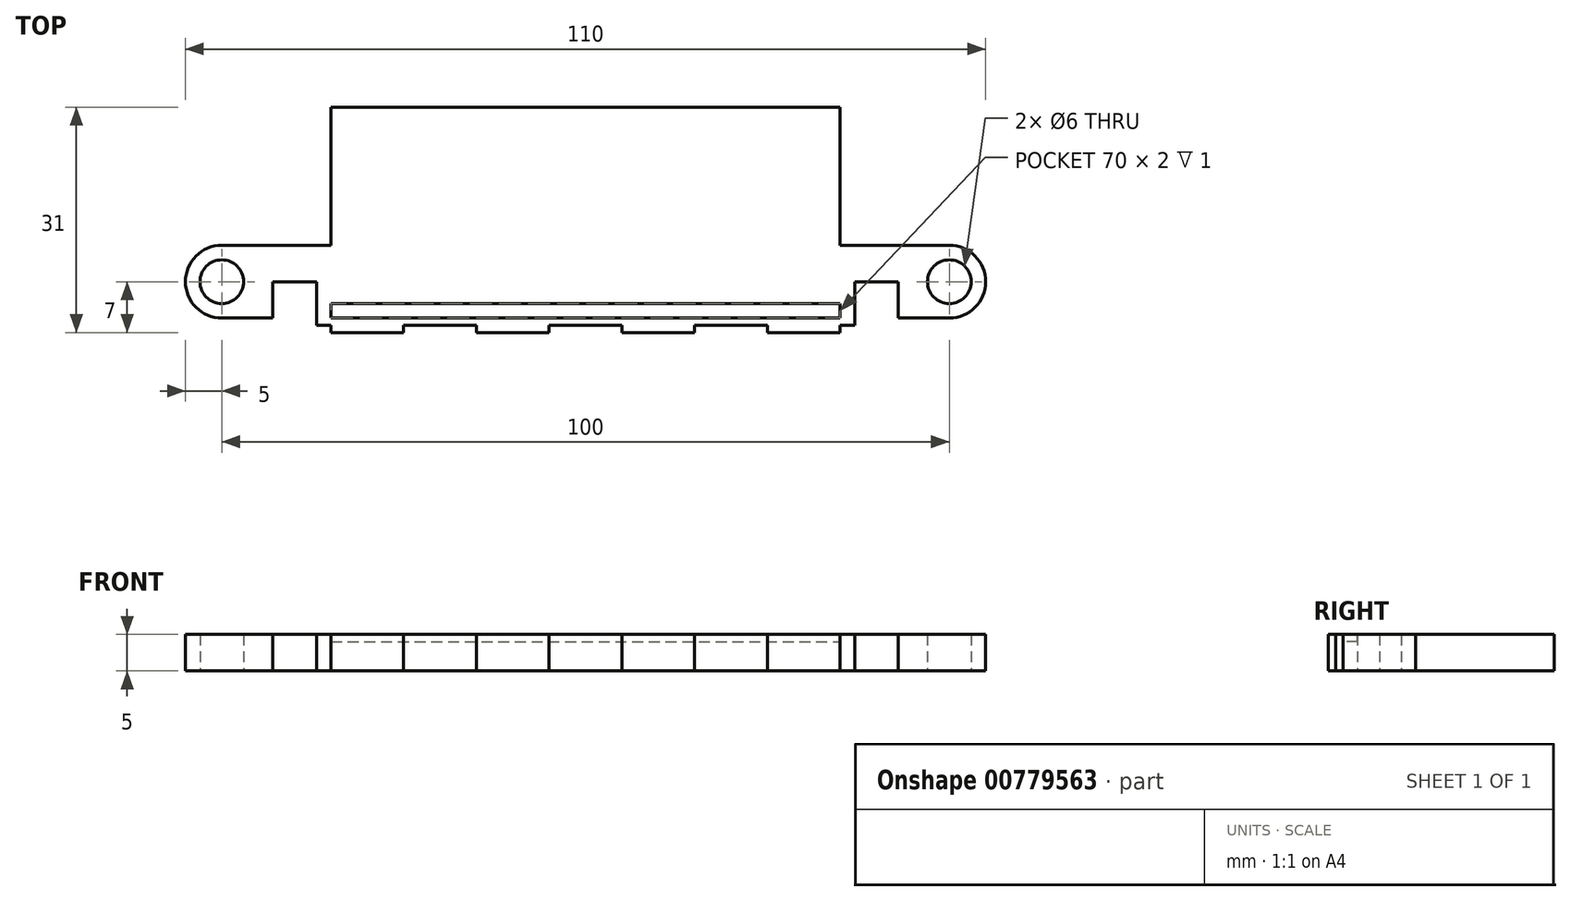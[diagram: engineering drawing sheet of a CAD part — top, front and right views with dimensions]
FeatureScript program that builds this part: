
annotation { "Feature Type Name" : "Feature", "Feature Type Description" : "" }
export const myFeature = defineFeature(function(context is Context, id is Id, definition is map)
    precondition{}
    {
        {
            assignVariable(context, id + "F0", {"name" : "MDF_thickness", "anyValue" : 5});
        }
        {
            var Q0;
            Q0=qCreatedBy(makeId("Top.planeOp"),FACE);
            var sketch = newSketch(context, id + "F1", { "sketchPlane" : qUnion([Q0])});
            skLineSegment(sketch, "E0.left", {"start": v(35, -16) * mm, "end": v(35, 15) * mm, "construction": true});
            skLineSegment(sketch, "E1", {"start": v(0, -15) * mm, "end": v(5, -15) * mm});
            skLineSegment(sketch, "E2", {"start": v(5, -15) * mm, "end": v(5, -16) * mm});
            skLineSegment(sketch, "E3", {"start": v(5, -16) * mm, "end": v(15, -16) * mm});
            skLineSegment(sketch, "E4", {"start": v(15, -16) * mm, "end": v(15, -15) * mm});
            skLineSegment(sketch, "E5", {"start": v(15, -15) * mm, "end": v(25, -15) * mm});
            skLineSegment(sketch, "E6", {"start": v(25, -15) * mm, "end": v(25, -16) * mm});
            skLineSegment(sketch, "E7", {"start": v(25, -16) * mm, "end": v(35, -16) * mm});
            skLineSegment(sketch, "E8", {"start": v(35, -16) * mm, "end": v(35, -15) * mm});
            skArc(sketch, "E9", {"start": v(50, -14) * mm, "mid": v(55, -9) * mm, "end": v(50, -4) * mm});
            skCircle(sketch, "E10", {"center": v(50, -9) * mm, "radius": 3 * mm});
            skLineSegment(sketch, "E11", {"start": v(50, -4) * mm, "end": v(35, -4) * mm});
            skLineSegment(sketch, "E12", {"start": v(45, -4) * mm, "end": v(45, -14) * mm, "construction": true});
            skLineSegment(sketch, "E13", {"start": v(35, -4) * mm, "end": v(35, 15) * mm});
            skLineSegment(sketch, "E14", {"start": v(35, 15) * mm, "end": v(0, 15) * mm});
            skLineSegment(sketch, "E15", {"start": v(50, -14) * mm, "end": v(45, -14) * mm});
            skLineSegment(sketch, "E16", {"start": v(45, -14) * mm, "end": v(43, -14) * mm});
            skLineSegment(sketch, "E17", {"start": v(43, -14) * mm, "end": v(43, -9) * mm});
            skLineSegment(sketch, "E18", {"start": v(43, -9) * mm, "end": v(37, -9) * mm});
            skLineSegment(sketch, "E19", {"start": v(37, -9) * mm, "end": v(37, -14) * mm});
            skLineSegment(sketch, "E20", {"start": v(35, -15) * mm, "end": v(37, -15) * mm});
            skLineSegment(sketch, "E21", {"start": v(37, -15) * mm, "end": v(37, -14) * mm});
            skLineSegment(sketch, "E22.MirrorCS", {"start": v(-35, 15) * mm, "end": v(0, 15) * mm});
            skLineSegment(sketch, "E23.MirrorCS", {"start": v(0, -15) * mm, "end": v(-5, -15) * mm});
            skLineSegment(sketch, "E24.MirrorCS", {"start": v(-35, -16) * mm, "end": v(-35, -15) * mm});
            skLineSegment(sketch, "E25.MirrorCS", {"start": v(-35, -15) * mm, "end": v(-37, -15) * mm});
            skLineSegment(sketch, "E26.MirrorCS", {"start": v(-45, -14) * mm, "end": v(-43, -14) * mm});
            skLineSegment(sketch, "E27.MirrorCS", {"start": v(-15, -16) * mm, "end": v(-15, -15) * mm});
            skLineSegment(sketch, "E28.MirrorCS", {"start": v(-37, -15) * mm, "end": v(-37, -14) * mm});
            skLineSegment(sketch, "E29.MirrorCS", {"start": v(-25, -15) * mm, "end": v(-25, -16) * mm});
            skLineSegment(sketch, "E30.MirrorCS", {"start": v(-5, -15) * mm, "end": v(-5, -16) * mm});
            skLineSegment(sketch, "E31.MirrorCS", {"start": v(-50, -14) * mm, "end": v(-45, -14) * mm});
            skLineSegment(sketch, "E32.MirrorCS", {"start": v(-35, -4) * mm, "end": v(-35, 15) * mm});
            skArc(sketch, "E33.MirrorCS", {"start": v(-50, -14) * mm, "mid": v(-55, -9) * mm, "end": v(-50, -4) * mm});
            skLineSegment(sketch, "E34.MirrorCS", {"start": v(-5, -16) * mm, "end": v(-15, -16) * mm});
            skLineSegment(sketch, "E35.MirrorCS", {"start": v(-45, -4) * mm, "end": v(-45, -14) * mm, "construction": true});
            skLineSegment(sketch, "E36.MirrorCS", {"start": v(-35, -16) * mm, "end": v(-35, 15) * mm, "construction": true});
            skLineSegment(sketch, "E37.MirrorCS", {"start": v(-15, -15) * mm, "end": v(-25, -15) * mm});
            skLineSegment(sketch, "E38.MirrorCS", {"start": v(-25, -16) * mm, "end": v(-35, -16) * mm});
            skLineSegment(sketch, "E39.MirrorCS", {"start": v(-43, -9) * mm, "end": v(-37, -9) * mm});
            skLineSegment(sketch, "E40.MirrorCS", {"start": v(-37, -9) * mm, "end": v(-37, -14) * mm});
            skCircle(sketch, "E41.MirrorC", {"center": v(-50, -9) * mm, "radius": 3 * mm});
            skLineSegment(sketch, "E42.MirrorCS", {"start": v(-50, -4) * mm, "end": v(-35, -4) * mm});
            skLineSegment(sketch, "E43.MirrorCS", {"start": v(-43, -14) * mm, "end": v(-43, -9) * mm});
            skSolve(sketch);
        }
        {
            var Q0;
            Q0 = qSketchRegion(id + "F1", true);
            extrude(context, id + "F2", {"entities" : qUnion([Q0]), "depth" : (getVariable(context, 'MDF_thickness')) * mm, "offsetDistance" : 25 * mm});
        }
        {
            var Q0;
            Q0=makeQuery(id+"F2.opExtrude","CAP_FACE",FACE,{"disambiguationData":[OSD([sQuery(id+"F1.wireOp",EDGE,"E1"),sQuery(id+"F1.wireOp",EDGE,"E2"),sQuery(id+"F1.wireOp",EDGE,"E3"),sQuery(id+"F1.wireOp",EDGE,"E4"),sQuery(id+"F1.wireOp",EDGE,"E5"),sQuery(id+"F1.wireOp",EDGE,"E6"),sQuery(id+"F1.wireOp",EDGE,"E7"),sQuery(id+"F1.wireOp",EDGE,"E8"),sQuery(id+"F1.wireOp",EDGE,"E9"),sQuery(id+"F1.wireOp",EDGE,"E10"),sQuery(id+"F1.wireOp",EDGE,"E11"),sQuery(id+"F1.wireOp",EDGE,"E13"),sQuery(id+"F1.wireOp",EDGE,"E14"),sQuery(id+"F1.wireOp",EDGE,"E15"),sQuery(id+"F1.wireOp",EDGE,"E16"),sQuery(id+"F1.wireOp",EDGE,"E17"),sQuery(id+"F1.wireOp",EDGE,"E18"),sQuery(id+"F1.wireOp",EDGE,"E19"),sQuery(id+"F1.wireOp",EDGE,"oVFt1hSz-rF75-tQqa-whk6-lmqHoJ6cugXr"),sQuery(id+"F1.wireOp",EDGE,"75e155fa-2116-4a00-8d93-47b2ce3b5e2c0.MirrorCS"),sQuery(id+"F1.wireOp",EDGE,"75e155fa-2116-4a00-8d93-47b2ce3b5e2c1.MirrorCS"),sQuery(id+"F1.wireOp",EDGE,"75e155fa-2116-4a00-8d93-47b2ce3b5e2c2.MirrorCS"),sQuery(id+"F1.wireOp",EDGE,"75e155fa-2116-4a00-8d93-47b2ce3b5e2c3.MirrorCS"),sQuery(id+"F1.wireOp",EDGE,"75e155fa-2116-4a00-8d93-47b2ce3b5e2c4.MirrorCS"),sQuery(id+"F1.wireOp",EDGE,"75e155fa-2116-4a00-8d93-47b2ce3b5e2c5.MirrorCS"),sQuery(id+"F1.wireOp",EDGE,"75e155fa-2116-4a00-8d93-47b2ce3b5e2c6.MirrorCS"),sQuery(id+"F1.wireOp",EDGE,"75e155fa-2116-4a00-8d93-47b2ce3b5e2c7.MirrorCS"),sQuery(id+"F1.wireOp",EDGE,"75e155fa-2116-4a00-8d93-47b2ce3b5e2c8.MirrorCS"),sQuery(id+"F1.wireOp",EDGE,"75e155fa-2116-4a00-8d93-47b2ce3b5e2c9.MirrorC"),sQuery(id+"F1.wireOp",EDGE,"75e155fa-2116-4a00-8d93-47b2ce3b5e2c10.MirrorCS"),sQuery(id+"F1.wireOp",EDGE,"75e155fa-2116-4a00-8d93-47b2ce3b5e2c11.MirrorCS"),sQuery(id+"F1.wireOp",EDGE,"75e155fa-2116-4a00-8d93-47b2ce3b5e2c12.MirrorCS"),sQuery(id+"F1.wireOp",EDGE,"75e155fa-2116-4a00-8d93-47b2ce3b5e2c15.MirrorCS"),sQuery(id+"F1.wireOp",EDGE,"75e155fa-2116-4a00-8d93-47b2ce3b5e2c16.MirrorCS"),sQuery(id+"F1.wireOp",EDGE,"75e155fa-2116-4a00-8d93-47b2ce3b5e2c17.MirrorCS"),sQuery(id+"F1.wireOp",EDGE,"75e155fa-2116-4a00-8d93-47b2ce3b5e2c18.MirrorCS"),sQuery(id+"F1.wireOp",EDGE,"75e155fa-2116-4a00-8d93-47b2ce3b5e2c19.MirrorCS"),sQuery(id+"F1.wireOp",EDGE,"75e155fa-2116-4a00-8d93-47b2ce3b5e2c20.MirrorCS")])],"isStart":false});
            var sketch = newSketch(context, id + "F3", { "sketchPlane" : qUnion([Q0])});
            skLineSegment(sketch, "E44.bottom", {"start": v(-35, -12) * mm, "end": v(35, -12) * mm});
            skLineSegment(sketch, "E44.top", {"start": v(-35, -14) * mm, "end": v(35, -14) * mm});
            skLineSegment(sketch, "E44.left", {"start": v(-35, -12) * mm, "end": v(-35, -14) * mm});
            skLineSegment(sketch, "E44.right", {"start": v(35, -12) * mm, "end": v(35, -14) * mm});
            skLineSegment(sketch, "E45.bottom", {"start": v(-35, -12) * mm, "end": v(-35, -12) * mm});
            skLineSegment(sketch, "E45.top", {"start": v(-35, -14) * mm, "end": v(-35, -14) * mm});
            skSolve(sketch);
        }
        {
            var Q0;
            Q0 = qSketchRegion(id + "F3", true);
            extrude(context, id + "F4", {"entities" : qUnion([Q0]), "operationType" : NewBodyOperationType.REMOVE, "oppositeDirection" : true, "depth" : (getVariable(context, 'MDF_thickness') / 5) * mm, "offsetDistance" : 25 * mm});
        }
    });
